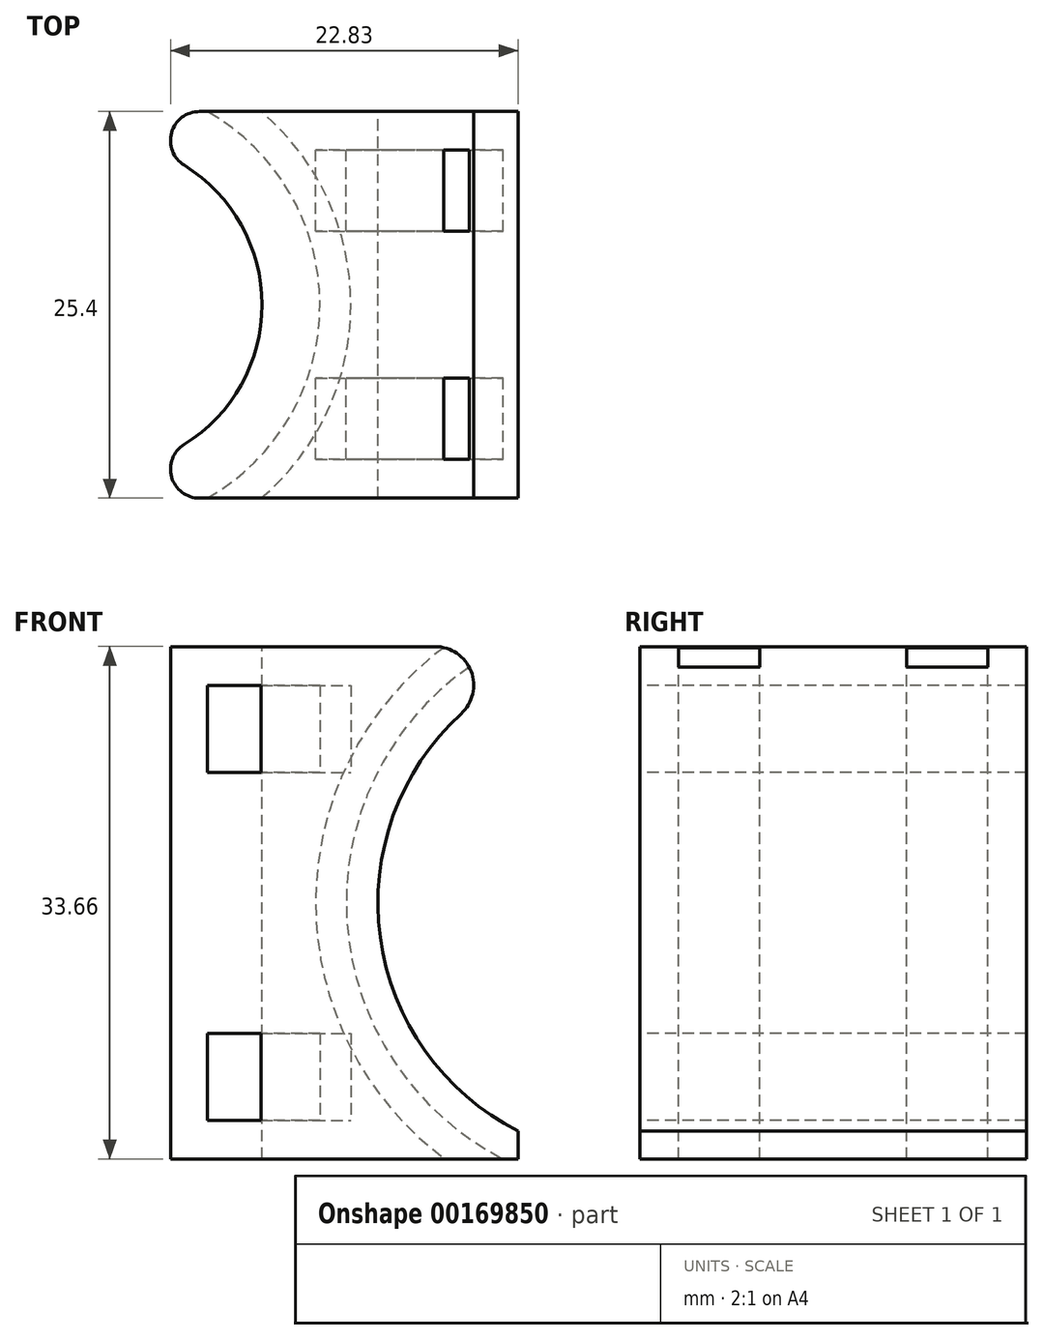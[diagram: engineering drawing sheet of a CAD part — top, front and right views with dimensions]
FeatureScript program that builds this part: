
annotation { "Feature Type Name" : "Feature", "Feature Type Description" : "" }
export const myFeature = defineFeature(function(context is Context, id is Id, definition is map)
    precondition{}
    {
        {
            var Q0;
            Q0=qCreatedBy(makeId("Front.planeOp"),FACE);
            var sketch = newSketch(context, id + "F0", { "sketchPlane" : qUnion([Q0])});
            skLineSegment(sketch, "E0", {"start": v(0, -16.83) * mm, "end": v(0, 16.83) * mm});
            skLineSegment(sketch, "E1", {"start": v(0, 0) * mm, "end": v(35.24, 0) * mm, "construction": true});
            skLineSegment(sketch, "E2", {"start": v(0, 16.83) * mm, "end": v(35.24, 16.83) * mm});
            skLineSegment(sketch, "E3.MirrorCS", {"start": v(0, -16.83) * mm, "end": v(35.24, -16.83) * mm});
            skLineSegment(sketch, "E4", {"start": v(10.8, 16.83) * mm, "end": v(10.8, -16.83) * mm, "construction": true});
            skArc(sketch, "E5", {"start": v(35.24, 16.83) * mm, "mid": v(18.41, 0) * mm, "end": v(35.24, -16.83) * mm});
            skArc(sketch, "E6", {"start": v(35.24, -16.83) * mm, "mid": v(52.07, 0) * mm, "end": v(35.24, 16.83) * mm, "construction": true});
            skSolve(sketch);
        }
        {
            var Q0;
            Q0=makeQuery(id+"F0.imprint","IMPRINT",FACE,{"disambiguationData":[TD([[makeQuery(id+"F0.imprint","IMPRINT",EDGE,{"derivedFrom":sQuery(id+"F0.wireOp",EDGE,"E0")}),-1.0]])]});
            var Q1;
            Q1=sQuery(id+"F0.wireOp",EDGE,"E6");
            extrude(context, id + "F1", {"entities" : qUnion([Q0]), "surfaceEntities" : qUnion([Q1]), "endBound" : BoundingType.SYMMETRIC, "depth" : 25.4 * mm});
        }
        {
            var Q0;
            Q0=qCreatedBy(makeId("Right.planeOp"),FACE);
            cPlane(context, id + "F2", {"entities" : qUnion([Q0]), "cplaneType" : CPlaneType.OFFSET, "offset" : 32.7 * mm, "width" : 152.4 * mm, "height" : 152.4 * mm});
        }
        {
            var Q0;
            Q0=qCreatedBy(makeId("Top.planeOp"),FACE);
            var sketch = newSketch(context, id + "F3", { "sketchPlane" : qUnion([Q0])});
            skLineSegment(sketch, "E7", {"start": v(0, 10.8) * mm, "end": v(0, -10.8) * mm, "construction": true});
            skArc(sketch, "E8", {"start": v(0, -10.8) * mm, "mid": v(10.8, 0) * mm, "end": v(0, 10.8) * mm});
            skLineSegment(sketch, "E9", {"start": v(0, 10.8) * mm, "end": v(0, -10.8) * mm});
            skSolve(sketch);
        }
        {
            var Q0;
            Q0 = qSketchRegion(id + "F3", true);
            extrude(context, id + "F4", {"entities" : qUnion([Q0]), "operationType" : NewBodyOperationType.REMOVE, "endBound" : BoundingType.THROUGH_ALL, "oppositeDirection" : true, "depth" : 25.4 * mm, "hasSecondDirection" : true, "secondDirectionBound" : SecondDirectionBoundingType.THROUGH_ALL, "secondDirectionOppositeDirection" : false, "secondDirectionDepth" : 25.4 * mm});
        }
        {
            var Q0;
            Q0=makeQuery(id+"F1.opExtrude","SWEPT_EDGE",EDGE,{"disambiguationData":[OSD([sQuery(id+"F0.wireOp",EDGE,"E2"),sQuery(id+"F0.wireOp",EDGE,"E5")])]});
            fillet(context, id + "F5", {"entities" : qUnion([Q0]), "radius" : 2.54 * mm, "tangentPropagation" : true, "allowEdgeOverflow" : false});
        }
        {
            var Q0;
            Q0=qCreatedBy(id+"F2.planeOp",FACE);
            var sketch = newSketch(context, id + "F6", { "sketchPlane" : qUnion([Q0])});
            skLineSegment(sketch, "E10.bottom", {"start": v(10.16, 20.76) * mm, "end": v(4.83, 20.76) * mm});
            skLineSegment(sketch, "E10.top", {"start": v(10.16, 18.73) * mm, "end": v(4.83, 18.73) * mm});
            skLineSegment(sketch, "E10.left", {"start": v(10.16, 20.76) * mm, "end": v(10.16, 18.73) * mm});
            skLineSegment(sketch, "E10.right", {"start": v(4.83, 20.76) * mm, "end": v(4.83, 18.73) * mm});
            skLineSegment(sketch, "E11.MirrorCS", {"start": v(-10.16, 20.76) * mm, "end": v(-4.83, 20.76) * mm});
            skLineSegment(sketch, "E12.MirrorCS", {"start": v(-10.16, 20.76) * mm, "end": v(-10.16, 18.73) * mm});
            skLineSegment(sketch, "E13.MirrorCS", {"start": v(-10.16, 18.73) * mm, "end": v(-4.83, 18.73) * mm});
            skLineSegment(sketch, "E14.MirrorCS", {"start": v(-4.83, 20.76) * mm, "end": v(-4.83, 18.73) * mm});
            skSolve(sketch);
        }
        {
            var Q0;
            Q0 = qSketchRegion(id + "F6", true);
            var Q1;
            Q1=makeQuery(id+"F1.opExtrude","SWEPT_FACE",FACE,{"disambiguationData":[OSD([sQuery(id+"F0.wireOp",EDGE,"E5")])]});
            revolve(context, id + "F7", {"operationType" : NewBodyOperationType.REMOVE, "entities" : qUnion([Q0]), "axis" : qUnion([Q1]), "revolveType" : RevolveType.FULL});
        }
        {
            var Q0;
            Q0=qCreatedBy(makeId("Front.planeOp"),FACE);
            var sketch = newSketch(context, id + "F8", { "sketchPlane" : qUnion([Q0])});
            skLineSegment(sketch, "E15.bottom", {"start": v(27.62, -14.29) * mm, "end": v(35.24, -14.29) * mm});
            skLineSegment(sketch, "E15.top", {"start": v(27.62, -16.83) * mm, "end": v(35.24, -16.83) * mm});
            skLineSegment(sketch, "E15.left", {"start": v(27.62, -14.29) * mm, "end": v(27.62, -16.83) * mm});
            skLineSegment(sketch, "E15.right", {"start": v(35.24, -14.29) * mm, "end": v(35.24, -16.83) * mm});
            skSolve(sketch);
        }
        {
            var Q0;
            Q0 = qSketchRegion(id + "F8", true);
            extrude(context, id + "F9", {"entities" : qUnion([Q0]), "operationType" : NewBodyOperationType.REMOVE, "endBound" : BoundingType.THROUGH_ALL, "depth" : 25.4 * mm, "hasSecondDirection" : true, "secondDirectionBound" : SecondDirectionBoundingType.THROUGH_ALL, "secondDirectionOppositeDirection" : true, "secondDirectionDepth" : 25.4 * mm});
        }
        {
            var Q0;
            Q0=qCreatedBy(makeId("Right.planeOp"),FACE);
            var sketch = newSketch(context, id + "F10", { "sketchPlane" : qUnion([Q0])});
            skLineSegment(sketch, "E16.bottom", {"start": v(-14.6, 14.29) * mm, "end": v(-16.64, 14.29) * mm});
            skLineSegment(sketch, "E16.top", {"start": v(-14.6, 8.57) * mm, "end": v(-16.64, 8.57) * mm});
            skLineSegment(sketch, "E16.left", {"start": v(-14.6, 14.29) * mm, "end": v(-14.6, 8.57) * mm});
            skLineSegment(sketch, "E16.right", {"start": v(-16.64, 14.29) * mm, "end": v(-16.64, 8.57) * mm});
            skLineSegment(sketch, "E17.MirrorCS", {"start": v(-14.6, -8.57) * mm, "end": v(-16.64, -8.57) * mm});
            skLineSegment(sketch, "E18.MirrorCS", {"start": v(-14.6, -14.29) * mm, "end": v(-14.6, -8.57) * mm});
            skLineSegment(sketch, "E19.MirrorCS", {"start": v(-14.6, -14.29) * mm, "end": v(-16.64, -14.29) * mm});
            skLineSegment(sketch, "E20.MirrorCS", {"start": v(-16.64, -14.29) * mm, "end": v(-16.64, -8.57) * mm});
            skSolve(sketch);
        }
        {
            var Q0;
            Q0 = qSketchRegion(id + "F10", true);
            var Q1;
            Q1=makeQuery(id+"F4.boolean.opBoolean","COPY",FACE,{"derivedFrom":makeQuery(id+"F4.opExtrude","SWEPT_FACE",FACE,{"disambiguationData":[OSD([sQuery(id+"F3.wireOp",EDGE,"E8")])]})});
            revolve(context, id + "F11", {"operationType" : NewBodyOperationType.REMOVE, "entities" : qUnion([Q0]), "axis" : qUnion([Q1]), "revolveType" : RevolveType.FULL, "oppositeDirection" : true});
        }
        {
            var Q0;
            Q0=makeQuery(id+"F1.opExtrude","SWEPT_FACE",FACE,{"disambiguationData":[OSD([sQuery(id+"F0.wireOp",EDGE,"E2")])]});
            var sketch = newSketch(context, id + "F12", { "sketchPlane" : qUnion([Q0])});
            skLineSegment(sketch, "E21", {"start": v(0, 12.7) * mm, "end": v(5.69, 9.18) * mm});
            skLineSegment(sketch, "E22", {"start": v(5.69, 9.18) * mm, "end": v(0, 9.18) * mm});
            skLineSegment(sketch, "E23", {"start": v(0, 9.18) * mm, "end": v(0, 12.7) * mm});
            skLineSegment(sketch, "E24.MirrorCS", {"start": v(0, -9.18) * mm, "end": v(0, -12.7) * mm});
            skLineSegment(sketch, "E25.MirrorCS", {"start": v(5.69, -9.18) * mm, "end": v(0, -9.18) * mm});
            skLineSegment(sketch, "E26.MirrorCS", {"start": v(0, -12.7) * mm, "end": v(5.69, -9.18) * mm});
            skSolve(sketch);
        }
        {
            var Q0;
            Q0 = qSketchRegion(id + "F12", true);
            extrude(context, id + "F13", {"entities" : qUnion([Q0]), "operationType" : NewBodyOperationType.REMOVE, "endBound" : BoundingType.THROUGH_ALL, "oppositeDirection" : true, "depth" : 25.4 * mm});
        }
        {
            var Q0;
            Q0=makeQuery(id+"F13.boolean.opBoolean","MERGE",EDGE,{"derivedFrom":[makeQuery(id+"F1.opExtrude","CAP_EDGE",EDGE,{"disambiguationData":[OSD([sQuery(id+"F0.wireOp",EDGE,"E0")])],"isStart":true}),makeQuery(id+"F13.opExtrude","SWEPT_EDGE",EDGE,{"disambiguationData":[OSD([sQuery(id+"F0.wireOp",EDGE,"E2"),sQuery(id+"F12.wireOp",EDGE,"E21"),sQuery(id+"F12.wireOp",EDGE,"E23")])]})]});
            var Q1;
            Q1=makeQuery(id+"F13.boolean.opBoolean","MERGE",EDGE,{"derivedFrom":[makeQuery(id+"F1.opExtrude","CAP_EDGE",EDGE,{"disambiguationData":[OSD([sQuery(id+"F0.wireOp",EDGE,"E0")])],"isStart":false}),makeQuery(id+"F13.opExtrude","SWEPT_EDGE",EDGE,{"disambiguationData":[OSD([sQuery(id+"F0.wireOp",EDGE,"E2"),sQuery(id+"F12.wireOp",EDGE,"E24.MirrorCS"),sQuery(id+"F12.wireOp",EDGE,"E26.MirrorCS")])]})]});
            fillet(context, id + "F14", {"entities" : qUnion([Q0, Q1]), "radius" : 1.9 * mm, "tangentPropagation" : true, "allowEdgeOverflow" : false});
        }
    });
